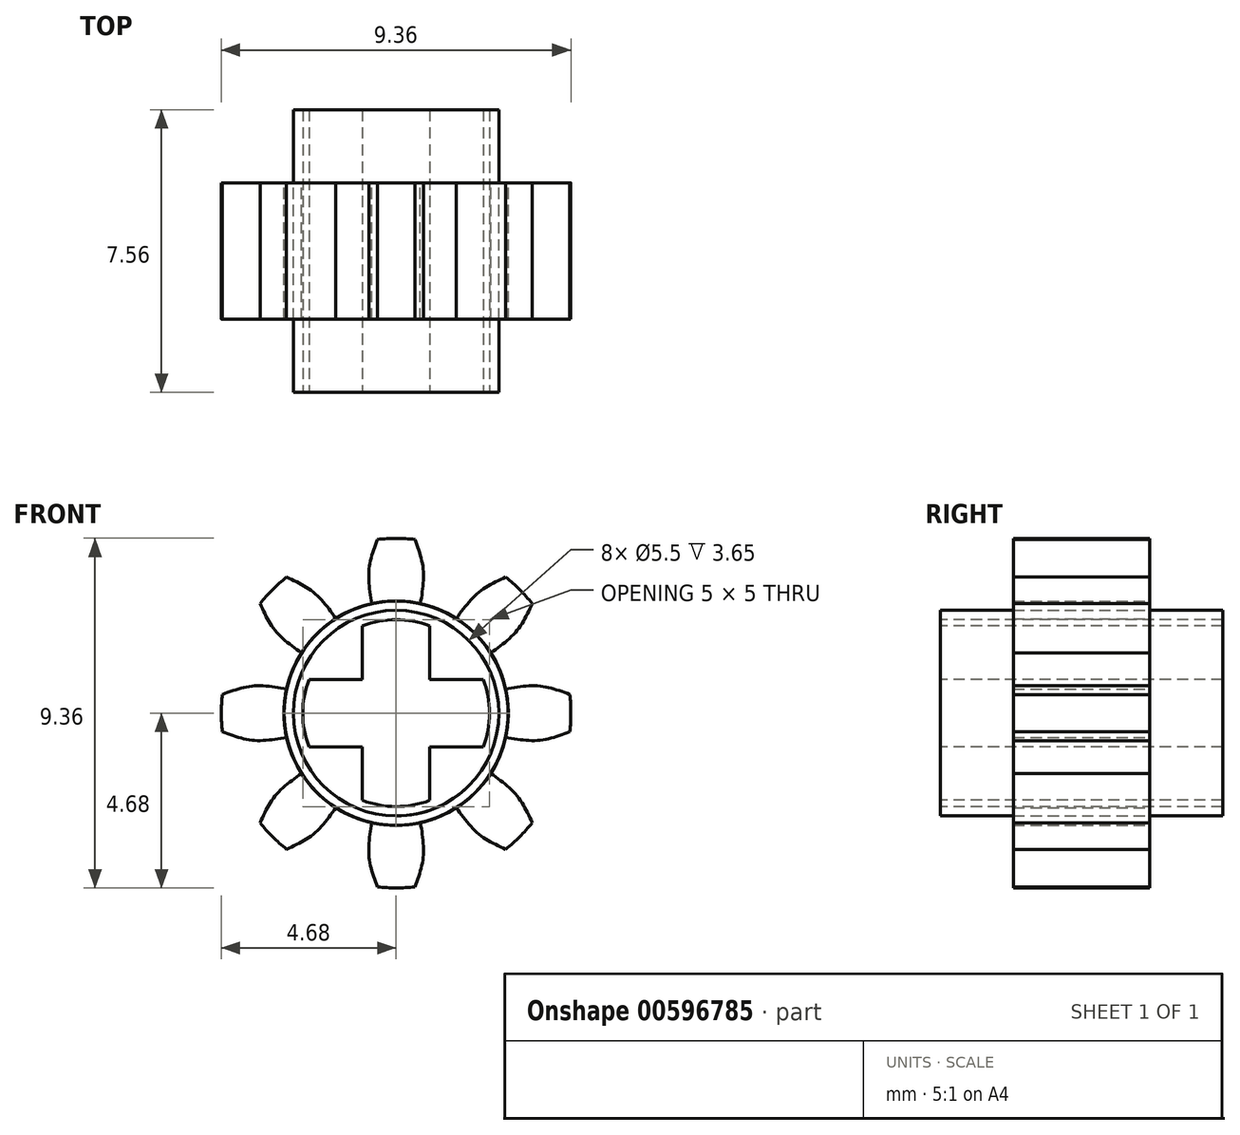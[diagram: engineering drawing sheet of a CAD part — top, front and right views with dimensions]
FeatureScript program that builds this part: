
annotation { "Feature Type Name" : "Feature", "Feature Type Description" : "" }
export const myFeature = defineFeature(function(context is Context, id is Id, definition is map)
    precondition{}
    {
        {
            var Q0;
            Q0=qCreatedBy(makeId("Front.planeOp"),FACE);
            var sketch = newSketch(context, id + "F0", { "sketchPlane" : qUnion([Q0])});
            skCircle(sketch, "E0", {"center": v(0, 0) * mm, "radius": 4.68 * mm});
            skCircle(sketch, "E1", {"center": v(0, 0) * mm, "radius": 3 * mm});
            skLineSegment(sketch, "E2", {"start": v(-0.72, 2.91) * mm, "end": v(0, 2.91) * mm, "construction": true});
            skLineSegment(sketch, "E3", {"start": v(0, 2.91) * mm, "end": v(0.72, 2.91) * mm, "construction": true});
            skLineSegment(sketch, "E4", {"start": v(-0.65, 2.93) * mm, "end": v(0, 2.93) * mm, "construction": true});
            skLineSegment(sketch, "E5", {"start": v(0, 2.93) * mm, "end": v(0.65, 2.93) * mm, "construction": true});
            skLineSegment(sketch, "E6", {"start": v(-0.5, 4.65) * mm, "end": v(0, 4.65) * mm, "construction": true});
            skLineSegment(sketch, "E7", {"start": v(0, 4.65) * mm, "end": v(0.5, 4.65) * mm, "construction": true});
            skLineSegment(sketch, "E8", {"start": v(0, 3) * mm, "end": v(0, 4.68) * mm, "construction": true});
            skLineSegment(sketch, "E9", {"start": v(0.86, 3.84) * mm, "end": v(-1.06, 3.84) * mm, "construction": true});
            skPoint(sketch, "E9.startSnap0", {"position": v(0, 3.84) * mm});
            skLineSegment(sketch, "E10", {"start": v(-0.72, 2.91) * mm, "end": v(-0.73, 5.4) * mm, "construction": true});
            skLineSegment(sketch, "E11", {"start": v(0.73, 2.91) * mm, "end": v(0.73, 5.27) * mm, "construction": true});
            skFitSpline(sketch, "E12", {"points": [v(-0.5, 4.65) * mm, v(-0.73, 3.84) * mm, v(-0.65, 2.93) * mm], "startDerivative": vector(-0.6, -1.62) * mm, "endDerivative": vector(0.3, -1.81) * mm});
            skFitSpline(sketch, "E13", {"points": [v(0.5, 4.65) * mm, v(0.73, 3.84) * mm, v(0.65, 2.93) * mm], "startDerivative": vector(0.6, -1.62) * mm, "endDerivative": vector(-0.3, -1.81) * mm});
            skCircle(sketch, "E14", {"center": v(0, 0) * mm, "radius": 2.75 * mm});
            skSolve(sketch);
        }
        {
            var Q0;
            {var subQ0=sQuery(id+"F0.wireOp",EDGE,"E12");Q0=makeQuery(id+"F0.imprint","IMPRINT",FACE,{"disambiguationData":[TD([[makeQuery(id+"F0.imprint","IMPRINT",EDGE,{"derivedFrom":subQ0}),1.0]])]});}
            var Q1;
            {var subQ0=sQuery(id+"F0.wireOp",EDGE,"E1");var subQ1=makeQuery(id+"F0.imprint","INTERSECT",VERTEX,{"derivedFrom":[subQ0,sQuery(id+"F0.wireOp",EDGE,"E12")]});Q1=makeQuery(id+"F0.imprint","IMPRINT",FACE,{"disambiguationData":[TD([[makeQuery(id+"F0.imprint","IMPRINT",EDGE,{"disambiguationData":[TD([[subQ1,1.0]])],"derivedFrom":subQ0}),1.0]])]});}
            extrude(context, id + "F1", {"entities" : qUnion([Q0, Q1]), "endBound" : BoundingType.SYMMETRIC, "depth" : 3.65 * mm, "offsetDistance" : 25 * mm});
        }
        {
            var Q0;
            Q0=makeQuery(id+"F1.opExtrude","CAP_FACE",FACE,{"disambiguationData":[OSD([sQuery(id+"F0.wireOp",EDGE,"E0"),sQuery(id+"F0.wireOp",EDGE,"E1"),sQuery(id+"F0.wireOp",EDGE,"E12"),sQuery(id+"F0.wireOp",EDGE,"E13")])],"isStart":false});
            var sketch = newSketch(context, id + "F2", { "sketchPlane" : qUnion([Q0])});
            skCircle(sketch, "E15", {"center": v(0, 0) * mm, "radius": 3 * mm});
            skFitSpline(sketch, "E16.0", {"points": [v(-0.5, 4.65) * mm, v(-0.6, 4.38) * mm, v(-0.8, 3.84) * mm, v(-0.7, 3.24) * mm, v(-0.65, 2.93) * mm]});
            skArc(sketch, "E17.0", {"start": v(0.5, 4.65) * mm, "mid": v(0, 4.68) * mm, "end": v(-0.5, 4.65) * mm});
            skFitSpline(sketch, "E18.0", {"points": [v(0.5, 4.65) * mm, v(0.6, 4.38) * mm, v(0.8, 3.84) * mm, v(0.7, 3.24) * mm, v(0.65, 2.93) * mm]});
            skSolve(sketch);
        }
        {
            var Q0;
            Q0=makeQuery(id+"F1.opExtrude","SWEPT_BODY",BODY,{"disambiguationData":[OSD([sQuery(id+"F0.wireOp",EDGE,"E0"),sQuery(id+"F0.wireOp",EDGE,"E1"),sQuery(id+"F0.wireOp",EDGE,"E12"),sQuery(id+"F0.wireOp",EDGE,"E13")])]});
            var Q1;
            Q1=sQuery(id+"F2.wireOp",EDGE,"E15");
            circularPattern(context, id + "F3", {"entities" : qUnion([Q0]), "axis" : qUnion([Q1]), "angle" : 360 * degree, "instanceCount" : 8, "equalSpace" : true});
        }
        {
            var Q0;
            Q0=makeQuery(id+"F0.imprint","IMPRINT",FACE,{"disambiguationData":[TD([[makeQuery(id+"F0.imprint","IMPRINT",EDGE,{"derivedFrom":sQuery(id+"F0.wireOp",EDGE,"E14")}),1.0]])]});
            extrude(context, id + "F4", {"entities" : qUnion([Q0]), "endBound" : BoundingType.SYMMETRIC, "depth" : 7.55 * mm, "offsetDistance" : 25 * mm});
        }
        {
            var Q0;
            Q0=makeQuery(id+"F4.opExtrude","CAP_FACE",FACE,{"disambiguationData":[OSD([sQuery(id+"F0.wireOp",EDGE,"E14")])],"isStart":false});
            var sketch = newSketch(context, id + "F5", { "sketchPlane" : qUnion([Q0])});
            skCircle(sketch, "E19", {"center": v(0, 0) * mm, "radius": 2.5 * mm});
            skLineSegment(sketch, "E20", {"start": v(0.9, -0.9) * mm, "end": v(0.9, -2.33) * mm});
            skLineSegment(sketch, "E21", {"start": v(0.9, 0.9) * mm, "end": v(0.9, 2.33) * mm});
            skLineSegment(sketch, "E22", {"start": v(0.9, 0.9) * mm, "end": v(2.33, 0.9) * mm});
            skLineSegment(sketch, "E23", {"start": v(0.9, -0.9) * mm, "end": v(2.33, -0.9) * mm});
            skLineSegment(sketch, "E24", {"start": v(-0.9, -0.9) * mm, "end": v(-0.9, -2.33) * mm});
            skLineSegment(sketch, "E25", {"start": v(-0.9, 0.9) * mm, "end": v(-0.9, 2.33) * mm});
            skLineSegment(sketch, "E26", {"start": v(-0.9, 0.9) * mm, "end": v(-2.33, 0.9) * mm});
            skLineSegment(sketch, "E27", {"start": v(-0.9, -0.9) * mm, "end": v(-2.33, -0.9) * mm});
            skLineSegment(sketch, "E28", {"start": v(0, 1.27) * mm, "end": v(0, -1.13) * mm, "construction": true});
            skLineSegment(sketch, "E29", {"start": v(-1.3, 0) * mm, "end": v(1.27, 0) * mm, "construction": true});
            skSolve(sketch);
        }
        {
            var Q0;
            {var subQ4=sQuery(id+"F5.wireOp",EDGE,"E20");Q0=makeQuery(id+"F5.imprint","IMPRINT",FACE,{"disambiguationData":[TD([[makeQuery(id+"F5.imprint","IMPRINT",EDGE,{"derivedFrom":subQ4}),-1.0]])]});}
            extrude(context, id + "F6", {"entities" : qUnion([Q0]), "operationType" : NewBodyOperationType.REMOVE, "endBound" : BoundingType.THROUGH_ALL, "oppositeDirection" : true, "depth" : 25 * mm, "offsetDistance" : 25 * mm});
        }
    });
